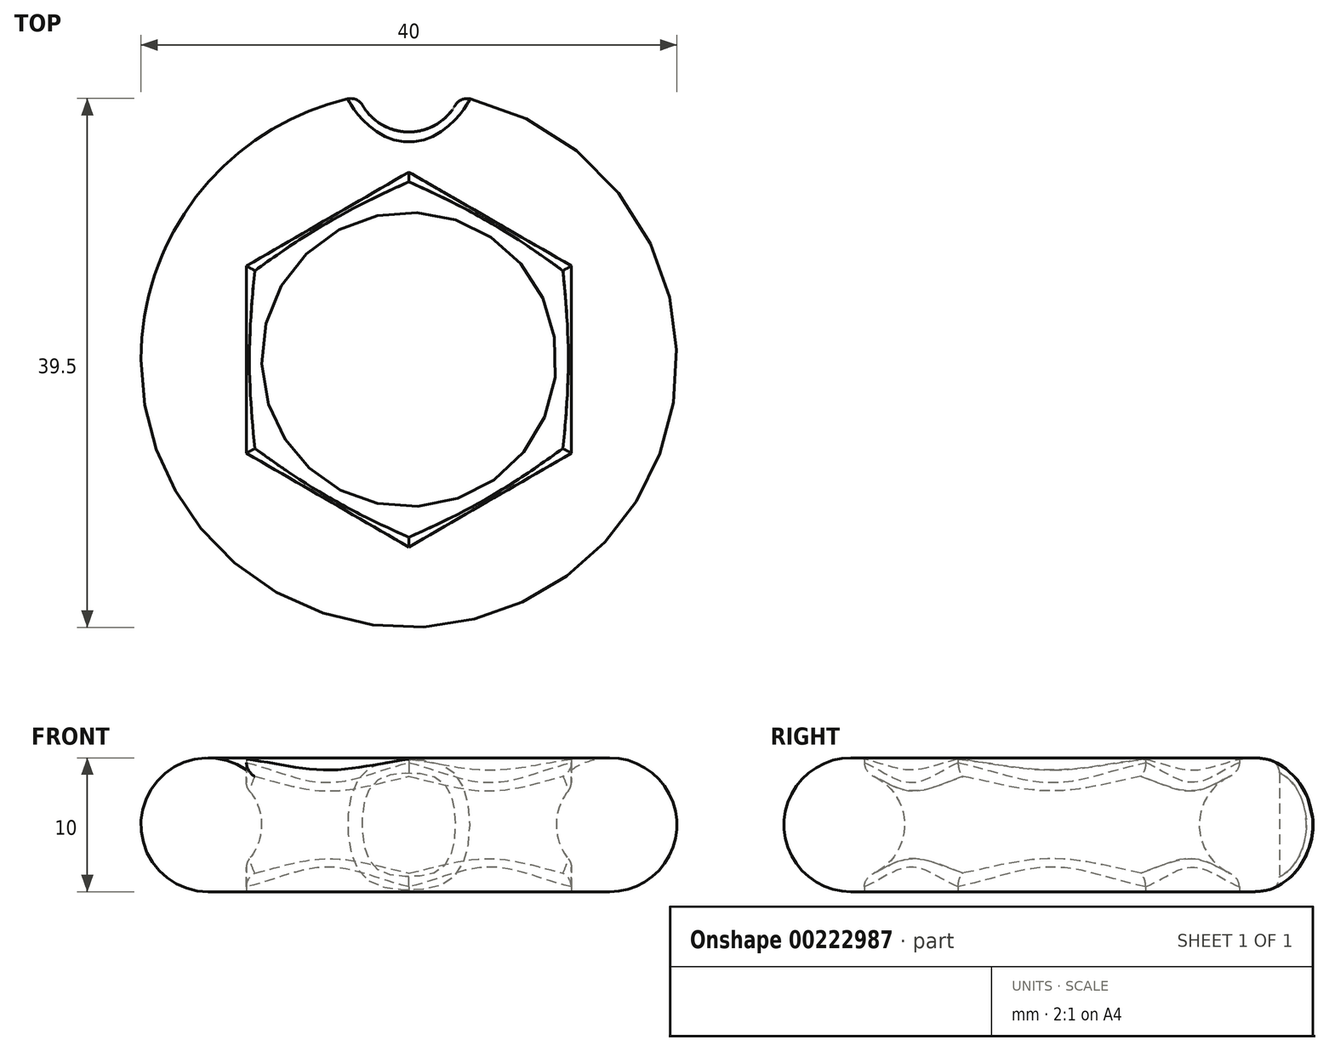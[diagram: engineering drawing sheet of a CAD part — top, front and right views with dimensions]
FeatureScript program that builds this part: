
annotation { "Feature Type Name" : "Feature", "Feature Type Description" : "" }
export const myFeature = defineFeature(function(context is Context, id is Id, definition is map)
    precondition{}
    {
        {
            var Q0;
            Q0=qCreatedBy(makeId("Front.planeOp"),FACE);
            var sketch = newSketch(context, id + "F0", { "sketchPlane" : qUnion([Q0])});
            skArc(sketch, "E0", {"start": v(-12, 9) * mm, "mid": v(-19.74, 6.58) * mm, "end": v(-15, 0) * mm});
            skArc(sketch, "E1", {"start": v(-12, 9) * mm, "mid": v(-6.32, 6.03) * mm, "end": v(0, 5) * mm});
            skLineSegment(sketch, "E2", {"start": v(-15, 0) * mm, "end": v(0, 0) * mm});
            skLineSegment(sketch, "E3", {"start": v(0, 0) * mm, "end": v(0, 5) * mm});
            skSolve(sketch);
        }
        {
            var Q0;
            Q0=makeQuery(id+"F0.imprint","IMPRINT",FACE,{"disambiguationData":[TD([[makeQuery(id+"F0.imprint","IMPRINT",EDGE,{"derivedFrom":sQuery(id+"F0.wireOp",EDGE,"E0")}),1.0]])]});
            var Q1;
            Q1=sQuery(id+"F0.wireOp",EDGE,"E3");
            revolve(context, id + "F1", {"entities" : qUnion([Q0]), "axis" : qUnion([Q1]), "revolveType" : RevolveType.FULL});
        }
        {
            var Q0;
            Q0=qCreatedBy(makeId("Top.planeOp"),FACE);
            var sketch = newSketch(context, id + "F2", { "sketchPlane" : qUnion([Q0])});
            skCircle(sketch, "E4", {"center": v(0, 21) * mm, "radius": 4 * mm});
            skSolve(sketch);
        }
        {
            var Q0;
            Q0=qCreatedBy(makeId("Top.planeOp"),FACE);
            var sketch = newSketch(context, id + "F3", { "sketchPlane" : qUnion([Q0])});
            skCircle(sketch, "E5.cCircle", {"center": v(0, 0) * mm, "radius": 14 * mm, "construction": true});
            skLineSegment(sketch, "E5.0", {"start": v(0, 14) * mm, "end": v(12.12, 7) * mm});
            skLineSegment(sketch, "E5.1", {"start": v(12.12, 7) * mm, "end": v(12.12, -7) * mm});
            skLineSegment(sketch, "E5.2", {"start": v(12.12, -7) * mm, "end": v(0, -14) * mm});
            skLineSegment(sketch, "E5.3", {"start": v(0, -14) * mm, "end": v(-12.12, -7) * mm});
            skLineSegment(sketch, "E5.4", {"start": v(-12.12, -7) * mm, "end": v(-12.12, 7) * mm});
            skLineSegment(sketch, "E5.5", {"start": v(-12.12, 7) * mm, "end": v(0, 14) * mm});
            skSolve(sketch);
        }
        {
            var Q0;
            Q0 = qSketchRegion(id + "F3", true);
            extrude(context, id + "F4", {"entities" : qUnion([Q0]), "operationType" : NewBodyOperationType.REMOVE, "depth" : 25 * mm});
        }
        {
            var Q0;
            Q0=qCreatedBy(makeId("Front.planeOp"),FACE);
            var sketch = newSketch(context, id + "F5", { "sketchPlane" : qUnion([Q0])});
            skCircle(sketch, "E6", {"center": v(-15, 5) * mm, "radius": 4 * mm});
            skSolve(sketch);
        }
        {
            var Q0;
            Q0 = qSketchRegion(id + "F5", true);
            var Q1;
            Q1=sQuery(id+"F0.wireOp",EDGE,"E3");
            revolve(context, id + "F6", {"operationType" : NewBodyOperationType.ADD, "entities" : qUnion([Q0]), "axis" : qUnion([Q1]), "revolveType" : RevolveType.FULL});
        }
        {
            var Q0;
            Q0=makeQuery(id+"F2.imprint","IMPRINT",FACE,{"disambiguationData":[TD([[makeQuery(id+"F2.imprint","IMPRINT",EDGE,{"derivedFrom":sQuery(id+"F2.wireOp",EDGE,"E4")}),1.0]])]});
            extrude(context, id + "F7", {"entities" : qUnion([Q0]), "operationType" : NewBodyOperationType.REMOVE, "depth" : 25 * mm});
        }
        {
            var Q0;
            Q0=makeQuery(id+"F7.boolean.opBoolean","INTERSECT",EDGE,{"derivedFrom":[makeQuery(id+"F1.opRevolve","SWEPT_FACE",FACE,{"disambiguationData":[OSD([sQuery(id+"F0.wireOp",EDGE,"E0")])]}),makeQuery(id+"F7.opExtrude","SWEPT_FACE",FACE,{"disambiguationData":[OSD([sQuery(id+"F2.wireOp",EDGE,"E4")])]})]});
            fillet(context, id + "F8", {"entities" : qUnion([Q0]), "radius" : 1 * mm, "tangentPropagation" : true, "allowEdgeOverflow" : false});
        }
        {
            var Q0;
            Q0=makeQuery(id+"F6.boolean.opBoolean","INTERSECT",EDGE,{"disambiguationData":[OD(1.0)],"derivedFrom":[makeQuery(id+"F4.boolean.opBoolean","COPY",FACE,{"derivedFrom":makeQuery(id+"F4.opExtrude","SWEPT_FACE",FACE,{"disambiguationData":[OSD([sQuery(id+"F3.wireOp",EDGE,"E5.5")])]})}),makeQuery(id+"F6.opRevolve","SWEPT_FACE",FACE,{"disambiguationData":[OSD([sQuery(id+"F5.wireOp",EDGE,"E6")])]})]});
            var Q1;
            Q1=makeQuery(id+"F6.boolean.opBoolean","INTERSECT",EDGE,{"disambiguationData":[OD(1.0)],"derivedFrom":[makeQuery(id+"F4.boolean.opBoolean","COPY",FACE,{"derivedFrom":makeQuery(id+"F4.opExtrude","SWEPT_FACE",FACE,{"disambiguationData":[OSD([sQuery(id+"F3.wireOp",EDGE,"E5.0")])]})}),makeQuery(id+"F6.opRevolve","SWEPT_FACE",FACE,{"disambiguationData":[OSD([sQuery(id+"F5.wireOp",EDGE,"E6")])]})]});
            var Q2;
            Q2=makeQuery(id+"F6.boolean.opBoolean","INTERSECT",EDGE,{"disambiguationData":[OD(1.0)],"derivedFrom":[makeQuery(id+"F4.boolean.opBoolean","COPY",FACE,{"derivedFrom":makeQuery(id+"F4.opExtrude","SWEPT_FACE",FACE,{"disambiguationData":[OSD([sQuery(id+"F3.wireOp",EDGE,"E5.4")])]})}),makeQuery(id+"F6.opRevolve","SWEPT_FACE",FACE,{"disambiguationData":[OSD([sQuery(id+"F5.wireOp",EDGE,"E6")])]})]});
            var Q3;
            Q3=makeQuery(id+"F6.boolean.opBoolean","INTERSECT",EDGE,{"disambiguationData":[OD(1.0)],"derivedFrom":[makeQuery(id+"F4.boolean.opBoolean","COPY",FACE,{"derivedFrom":makeQuery(id+"F4.opExtrude","SWEPT_FACE",FACE,{"disambiguationData":[OSD([sQuery(id+"F3.wireOp",EDGE,"E5.1")])]})}),makeQuery(id+"F6.opRevolve","SWEPT_FACE",FACE,{"disambiguationData":[OSD([sQuery(id+"F5.wireOp",EDGE,"E6")])]})]});
            var Q4;
            Q4=makeQuery(id+"F6.boolean.opBoolean","INTERSECT",EDGE,{"disambiguationData":[OD(1.0)],"derivedFrom":[makeQuery(id+"F4.boolean.opBoolean","COPY",FACE,{"derivedFrom":makeQuery(id+"F4.opExtrude","SWEPT_FACE",FACE,{"disambiguationData":[OSD([sQuery(id+"F3.wireOp",EDGE,"E5.3")])]})}),makeQuery(id+"F6.opRevolve","SWEPT_FACE",FACE,{"disambiguationData":[OSD([sQuery(id+"F5.wireOp",EDGE,"E6")])]})]});
            var Q5;
            Q5=makeQuery(id+"F6.boolean.opBoolean","INTERSECT",EDGE,{"disambiguationData":[OD(1.0)],"derivedFrom":[makeQuery(id+"F4.boolean.opBoolean","COPY",FACE,{"derivedFrom":makeQuery(id+"F4.opExtrude","SWEPT_FACE",FACE,{"disambiguationData":[OSD([sQuery(id+"F3.wireOp",EDGE,"E5.2")])]})}),makeQuery(id+"F6.opRevolve","SWEPT_FACE",FACE,{"disambiguationData":[OSD([sQuery(id+"F5.wireOp",EDGE,"E6")])]})]});
            var Q6;
            Q6=makeQuery(id+"F6.boolean.opBoolean","INTERSECT",EDGE,{"disambiguationData":[OD(0.0)],"derivedFrom":[makeQuery(id+"F4.boolean.opBoolean","COPY",FACE,{"derivedFrom":makeQuery(id+"F4.opExtrude","SWEPT_FACE",FACE,{"disambiguationData":[OSD([sQuery(id+"F3.wireOp",EDGE,"E5.5")])]})}),makeQuery(id+"F6.opRevolve","SWEPT_FACE",FACE,{"disambiguationData":[OSD([sQuery(id+"F5.wireOp",EDGE,"E6")])]})]});
            var Q7;
            Q7=makeQuery(id+"F6.boolean.opBoolean","INTERSECT",EDGE,{"disambiguationData":[OD(0.0)],"derivedFrom":[makeQuery(id+"F4.boolean.opBoolean","COPY",FACE,{"derivedFrom":makeQuery(id+"F4.opExtrude","SWEPT_FACE",FACE,{"disambiguationData":[OSD([sQuery(id+"F3.wireOp",EDGE,"E5.4")])]})}),makeQuery(id+"F6.opRevolve","SWEPT_FACE",FACE,{"disambiguationData":[OSD([sQuery(id+"F5.wireOp",EDGE,"E6")])]})]});
            var Q8;
            Q8=makeQuery(id+"F6.boolean.opBoolean","INTERSECT",EDGE,{"disambiguationData":[OD(0.0)],"derivedFrom":[makeQuery(id+"F4.boolean.opBoolean","COPY",FACE,{"derivedFrom":makeQuery(id+"F4.opExtrude","SWEPT_FACE",FACE,{"disambiguationData":[OSD([sQuery(id+"F3.wireOp",EDGE,"E5.0")])]})}),makeQuery(id+"F6.opRevolve","SWEPT_FACE",FACE,{"disambiguationData":[OSD([sQuery(id+"F5.wireOp",EDGE,"E6")])]})]});
            var Q9;
            Q9=makeQuery(id+"F6.boolean.opBoolean","INTERSECT",EDGE,{"disambiguationData":[OD(0.0)],"derivedFrom":[makeQuery(id+"F4.boolean.opBoolean","COPY",FACE,{"derivedFrom":makeQuery(id+"F4.opExtrude","SWEPT_FACE",FACE,{"disambiguationData":[OSD([sQuery(id+"F3.wireOp",EDGE,"E5.1")])]})}),makeQuery(id+"F6.opRevolve","SWEPT_FACE",FACE,{"disambiguationData":[OSD([sQuery(id+"F5.wireOp",EDGE,"E6")])]})]});
            var Q10;
            Q10=makeQuery(id+"F6.boolean.opBoolean","INTERSECT",EDGE,{"disambiguationData":[OD(0.0)],"derivedFrom":[makeQuery(id+"F4.boolean.opBoolean","COPY",FACE,{"derivedFrom":makeQuery(id+"F4.opExtrude","SWEPT_FACE",FACE,{"disambiguationData":[OSD([sQuery(id+"F3.wireOp",EDGE,"E5.2")])]})}),makeQuery(id+"F6.opRevolve","SWEPT_FACE",FACE,{"disambiguationData":[OSD([sQuery(id+"F5.wireOp",EDGE,"E6")])]})]});
            var Q11;
            Q11=makeQuery(id+"F6.boolean.opBoolean","INTERSECT",EDGE,{"disambiguationData":[OD(0.0)],"derivedFrom":[makeQuery(id+"F4.boolean.opBoolean","COPY",FACE,{"derivedFrom":makeQuery(id+"F4.opExtrude","SWEPT_FACE",FACE,{"disambiguationData":[OSD([sQuery(id+"F3.wireOp",EDGE,"E5.3")])]})}),makeQuery(id+"F6.opRevolve","SWEPT_FACE",FACE,{"disambiguationData":[OSD([sQuery(id+"F5.wireOp",EDGE,"E6")])]})]});
            fillet(context, id + "F9", {"entities" : qUnion([Q0, Q1, Q2, Q3, Q4, Q5, Q6, Q7, Q8, Q9, Q10, Q11]), "radius" : 1 * mm, "tangentPropagation" : true, "allowEdgeOverflow" : false});
        }
    });
